# Revit family: LAMP_SHOT 380 G2
name_source: partatom
category: Modelos genéricos
revit_build: Autodesk Revit 2018 (Build: 20190510_1515(x64)
units: mm (PartAtom-declared; Revit-internal decimal feet)

## family parameters
Anfitrión = Cara
Compartido = No
Corte con vacíos al cargar = No
Cota de conector redondo = Diámetro de uso
Puede alojar armadura = No
Punto de cálculo de habitación = No
Tipo de pieza = Normal

## types (12) — shared parameters
CRI = 80
Comentarios de tipo = Availability of tilting between -50º and 205º when placed in a project.
Elevación por defecto = 1219 mm
Fabricante = LAMP
Finish = Texturised grey
Gear = Electronic
Installation instructions = http://www.lamp.es
Insulation class = I
Lamp = HIGH POWER LED
Last update = 21/02/2022
Luminaire type = Outdoor - Spotlight
MacAdam = 3
Manufacturer URL = http://www.lamp.es
Manufacturer country = Spain
Manufacturer name = LAMP
Model explanation = Availability of tilting between -50º and 205º when placed in a project.
Power Supply = 220-240V 50/60Hz
Product URL = http://www.lamp.es
Product datasheet = http://www.lamp.es
Protection rating = IP65 / IK08
Type = HI POWER PHILIPS
Weight = 12.20 kg

## per-type parameters (varying)
| type | Descripción | Efficacy | Initial color | Initial intensity | LED Lifetime | Modelo | Photometric web file | Plum | Power | Product code |
| 4721LM 3000 SPOT | SHOT 380 G2 7000 8WW SP GR. | 92 lm/W | 3000 K | 4721 lm | 50.000 L90 B10 | SH23807SP830NG | Cabeza Shot : 4721LM 3000 SPOT | 51 W | 45 W | SH23807SP830NG |
| 4788LM 3000 MEDIUM FLOOD | SHOT 380 G2 7000 8WW MFL GR. | 94 lm/W | 3000 K | 4788 lm | 50.000 L90 B10 | SH23807MF830NG | Cabeza Shot : 4788LM 3000 MEDIUM FLOOD | 51 W | 45 W | SH23807MF830NG |
| 4920LM 3000 STREET | SHOT 380 G2 7000 8WW STREET GR. | 96 lm/W | 3000 K | 4920 lm | 50.000 L80 B10 | SH23807ST830NG | Cabeza Shot : 4920LM 3000 STREET | 51 W | 73 W | SH23807ST830NG |
| 4970LM 4000 SPOT | SHOT 380 G2 7000 8NW SP GR. | 97 lm/W | 4000 K | 4970 lm | 50.000 L90 B10 | SH23807SP840NG | Cabeza Shot : 4970LM 4000 SPOT | 51 W | 45 W | SH23807SP840NG |
| 5040LM 4000 MEDIUM FLOOD | SHOT 380 G2 7000 8NW MFL GR. | 99 lm/W | 4000 K | 5040 lm | 50.000 L90 B10 | SH23807MF840NG | Cabeza Shot : 5040LM 4000 MEDIUM FLOOD | 51 W | 45 W | SH23807MF840NG |
| 5179LM 4000 STREET | SHOT 380 G2 7000 8NW STREET GR. | 101 lm/W | 4000 K | 5179 lm | 50.000 L90 B10 | SH23807ST840NG | Cabeza Shot : 5179LM 4000 STREET | 51 W | 45 W | SH23807ST840NG |
| 7003LM 3000 SPOT | SHOT 380 G2 10500 8WW SP GR. | 85 lm/W | 3000 K | 7003 lm | 50.000 L80 B10 | SH23811SP830NG | Cabeza Shot : 7003LM 3000 SPOT | 83 W | 73 W | SH23811SP830NG |
| 7102LM 3000 MEDIUM FLOOD | SHOT 380 G2 10500 8WW MFL GR. | 86 lm/W | 3000 K | 7102 lm | 50.000 L80 B10 | SH23811MF830NG | Cabeza Shot : 7102LM 3000 MEDIUM FLOOD | 83 W | 73 W | SH23811MF830NG |
| 7297LM 3000 STREET | SHOT 380 G2 10500 8WW STREET GR. | 88 lm/W | 3000 K | 7297 lm | 50.000 L80 B10 | SH23811ST830NG | Cabeza Shot : 7297LM 3000 STREET | 83 W | 73 W | SH23811ST830NG |
| 7372LM 4000 SPOT | SHOT 380 G2 10500 8NW SP GR. | 89 lm/W | 4000 K | 7372 lm | 50.000 L80 B10 | SH23811SP840NG | Cabeza Shot : 7372LM 4000 SPOT | 83 W | 73 W | SH23811SP840NG |
| 7475LM 4000 MEDIUM FLOOD | SHOT 380 G2 10500 8NW MFL GR. | 91 lm/W | 4000 K | 7475 lm | 50.000 L80 B10 | SH23811MF840NG | Cabeza Shot : 7475LM 4000 MEDIUM FLOOD | 83 W | 73 W | SH23811MF840NG |
| 7682LM 4000 STREET | SHOT 380 G2 10500 8NW STREET GR. | 93 lm/W | 4000 K | 7682 lm | 50.000 L80 B10 | SH23811ST840NG | Cabeza Shot : 7682LM 4000 STREET | 83 W | 73 W | SH23811ST840NG |
